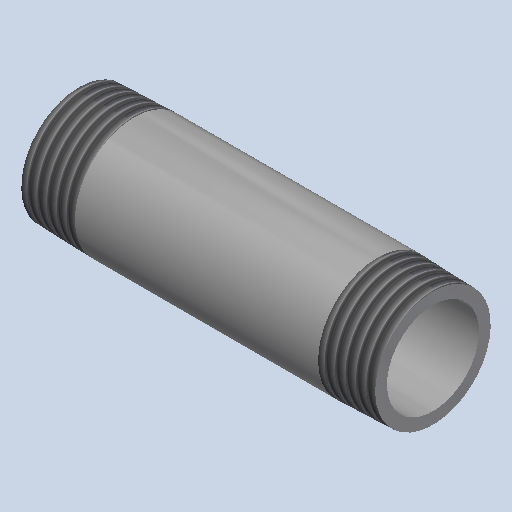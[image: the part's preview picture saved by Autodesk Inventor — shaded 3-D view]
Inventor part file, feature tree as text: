
AUTODESK INVENTOR PART (.ipt)
format: ipt  version: 2025 (Build 290162000, 162)  size: 217,600 bytes
history: native  units: mm (DEFAULTED — no unit token found)
features: other x8, revolve x1
ambient origin geometry x8: Origin, YZ Plane, XZ Plane, XY Plane, X Axis, Y Axis, Z Axis, Center Point
bodies: Solid1 (feature_tree)
feature tree (9):
  revolve  "Revolution1"  [1 undecoded]
  other  "Work Axis1"
  other  "Work Point5"
  other  "Work Axis2"
  other  "Work Point6"
  other  "Work Axis3"
  other  "Work Axis4"
  other  "Work Point7"
  other  "Work Point8"
note: 1 required parameter value undecoded (feature->parameter linkage not recoverable at this tier; creation-order binding heuristic only, values carry confidence <= 0.55)
